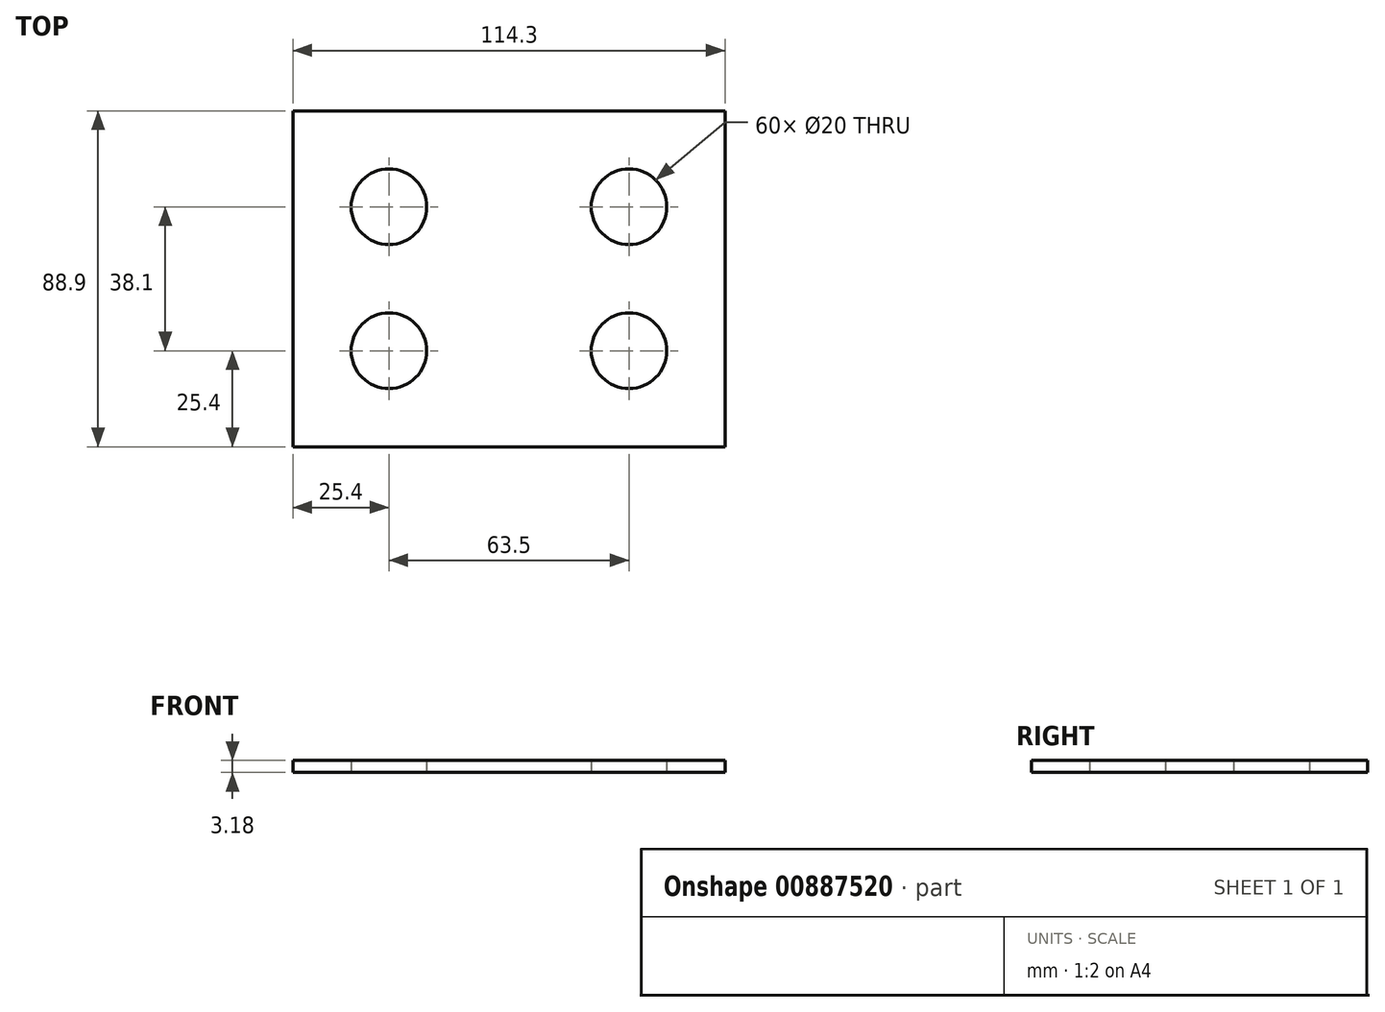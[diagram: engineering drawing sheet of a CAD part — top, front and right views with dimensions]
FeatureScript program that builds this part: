
annotation { "Feature Type Name" : "Feature", "Feature Type Description" : "" }
export const myFeature = defineFeature(function(context is Context, id is Id, definition is map)
    precondition{}
    {
        {
            var Q0;
            Q0=qCreatedBy(makeId("Top.planeOp"),FACE);
            var sketch = newSketch(context, id + "F0", { "sketchPlane" : qUnion([Q0])});
            skLineSegment(sketch, "E0.bottom", {"start": v(57.15, 44.45) * mm, "end": v(-57.15, 44.45) * mm});
            skLineSegment(sketch, "E0.top", {"start": v(57.15, -44.45) * mm, "end": v(-57.15, -44.45) * mm});
            skLineSegment(sketch, "E0.left", {"start": v(57.15, 44.45) * mm, "end": v(57.15, -44.45) * mm});
            skLineSegment(sketch, "E0.right", {"start": v(-57.15, 44.45) * mm, "end": v(-57.15, -44.45) * mm});
            skPoint(sketch, "E0.middle", {"position": v(0, 0) * mm});
            skLineSegment(sketch, "E1.bottom", {"start": v(-31.75, 19.05) * mm, "end": v(31.75, 19.05) * mm, "construction": true});
            skLineSegment(sketch, "E1.top", {"start": v(-31.75, -19.05) * mm, "end": v(31.75, -19.05) * mm, "construction": true});
            skLineSegment(sketch, "E1.left", {"start": v(-31.75, 19.05) * mm, "end": v(-31.75, -19.05) * mm, "construction": true});
            skLineSegment(sketch, "E1.right", {"start": v(31.75, 19.05) * mm, "end": v(31.75, -19.05) * mm, "construction": true});
            skCircle(sketch, "E2", {"center": v(31.75, 19.05) * mm, "radius": 10 * mm});
            skCircle(sketch, "E3", {"center": v(-31.75, 19.05) * mm, "radius": 10 * mm});
            skCircle(sketch, "E4", {"center": v(-31.75, -19.05) * mm, "radius": 10 * mm});
            skCircle(sketch, "E5", {"center": v(31.75, -19.05) * mm, "radius": 10 * mm});
            skSolve(sketch);
        }
        {
            var Q0;
            Q0 = qSketchRegion(id + "F0", true);
            extrude(context, id + "F1", {"entities" : qUnion([Q0]), "depth" : 3.17 * mm, "offsetDistance" : 25.4 * mm});
        }
    });
